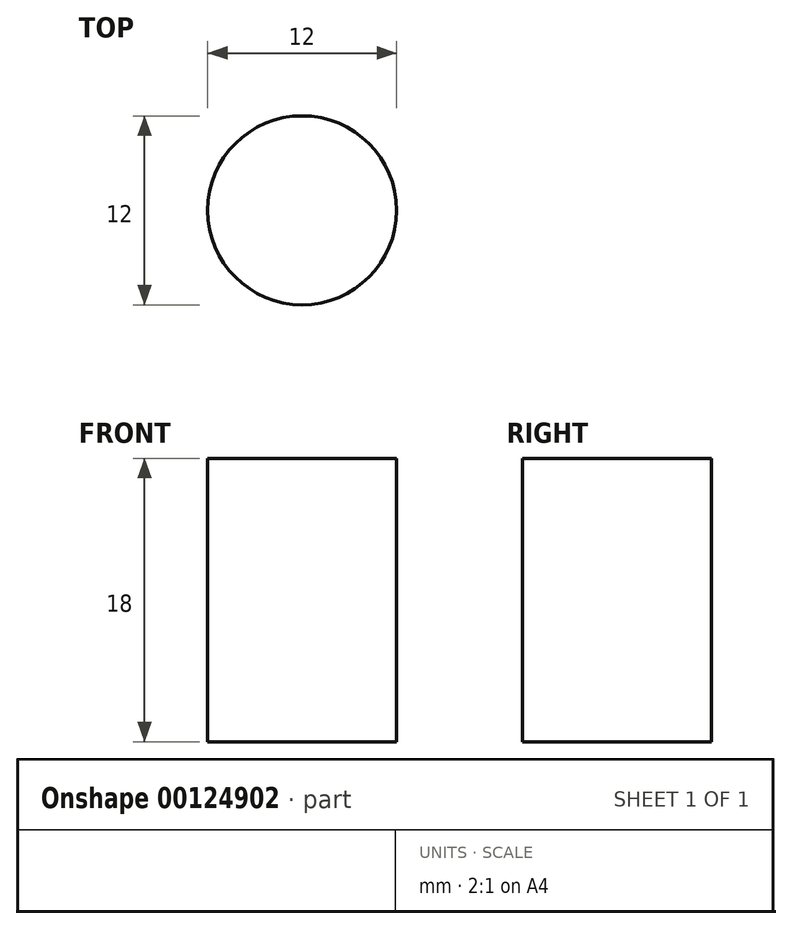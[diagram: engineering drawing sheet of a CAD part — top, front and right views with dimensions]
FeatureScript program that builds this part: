
annotation { "Feature Type Name" : "Feature", "Feature Type Description" : "" }
export const myFeature = defineFeature(function(context is Context, id is Id, definition is map)
    precondition{}
    {
        {
            var Q0;
            Q0=qCreatedBy(makeId("Top.planeOp"),FACE);
            var sketch = newSketch(context, id + "F0", { "sketchPlane" : qUnion([Q0])});
            skCircle(sketch, "E0", {"center": v(0, 0) * mm, "radius": 6 * mm});
            skSolve(sketch);
        }
        {
            var Q0;
            Q0=makeQuery(id+"F0.imprint","IMPRINT",FACE,{"disambiguationData":[TD([[makeQuery(id+"F0.imprint","IMPRINT",EDGE,{"derivedFrom":sQuery(id+"F0.wireOp",EDGE,"E0")}),1.0]])]});
            extrude(context, id + "F1", {"entities" : qUnion([Q0]), "depth" : 18 * mm});
        }
    });
